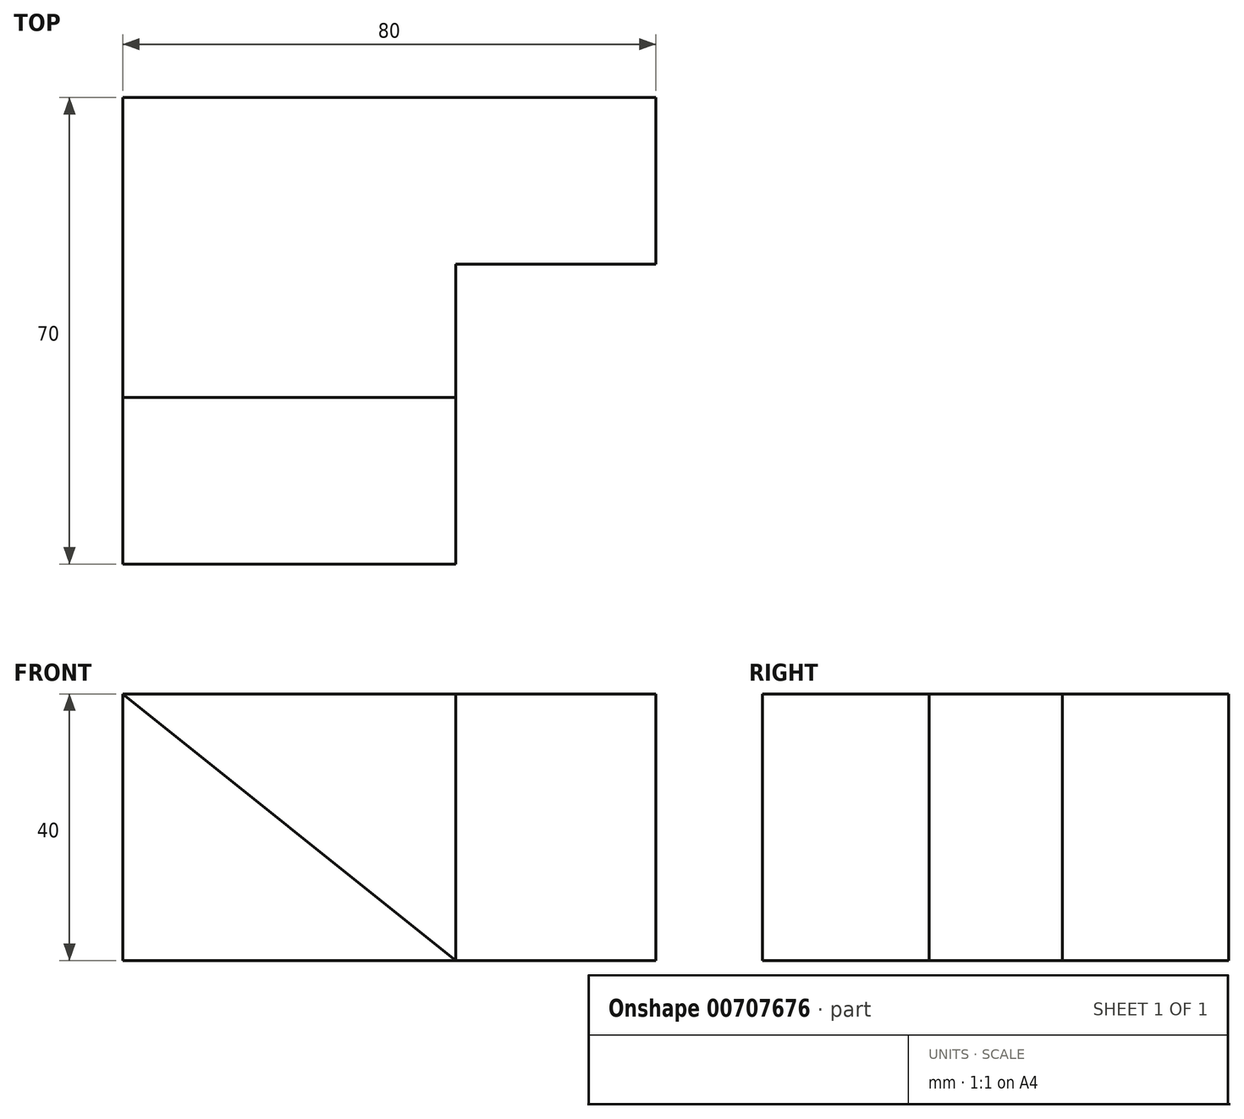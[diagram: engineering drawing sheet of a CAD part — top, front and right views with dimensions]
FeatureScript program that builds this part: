
annotation { "Feature Type Name" : "Feature", "Feature Type Description" : "" }
export const myFeature = defineFeature(function(context is Context, id is Id, definition is map)
    precondition{}
    {
        {
            var Q0;
            Q0=qCreatedBy(makeId("Front.planeOp"),FACE);
            var sketch = newSketch(context, id + "F0", { "sketchPlane" : qUnion([Q0])});
            skLineSegment(sketch, "E0", {"start": v(0, 0) * mm, "end": v(0, 40) * mm});
            skLineSegment(sketch, "E1", {"start": v(0, 0) * mm, "end": v(50, 0) * mm});
            skLineSegment(sketch, "E2", {"start": v(50, 0) * mm, "end": v(0, 40) * mm});
            skSolve(sketch);
        }
        {
            var Q0;
            Q0 = qSketchRegion(id + "F0", true);
            extrude(context, id + "F1", {"entities" : qUnion([Q0]), "depth" : 25 * mm, "offsetDistance" : 25 * mm});
        }
        {
            var Q0;
            Q0=qCreatedBy(makeId("Top.planeOp"),FACE);
            var sketch = newSketch(context, id + "F2", { "sketchPlane" : qUnion([Q0])});
            skLineSegment(sketch, "E3", {"start": v(0, 0) * mm, "end": v(0, 45) * mm});
            skLineSegment(sketch, "E4", {"start": v(0, 45) * mm, "end": v(80, 45) * mm});
            skLineSegment(sketch, "E5", {"start": v(80, 45) * mm, "end": v(80, 20) * mm});
            skLineSegment(sketch, "E6", {"start": v(0, 0) * mm, "end": v(50, 0) * mm});
            skLineSegment(sketch, "E7", {"start": v(80, 20) * mm, "end": v(50, 20) * mm});
            skLineSegment(sketch, "E8", {"start": v(50, 20) * mm, "end": v(50, 0) * mm});
            skSolve(sketch);
        }
        {
            var Q0;
            Q0 = qSketchRegion(id + "F2", true);
            extrude(context, id + "F3", {"entities" : qUnion([Q0]), "operationType" : NewBodyOperationType.ADD, "depth" : 40 * mm, "offsetDistance" : 25 * mm});
        }
    });
